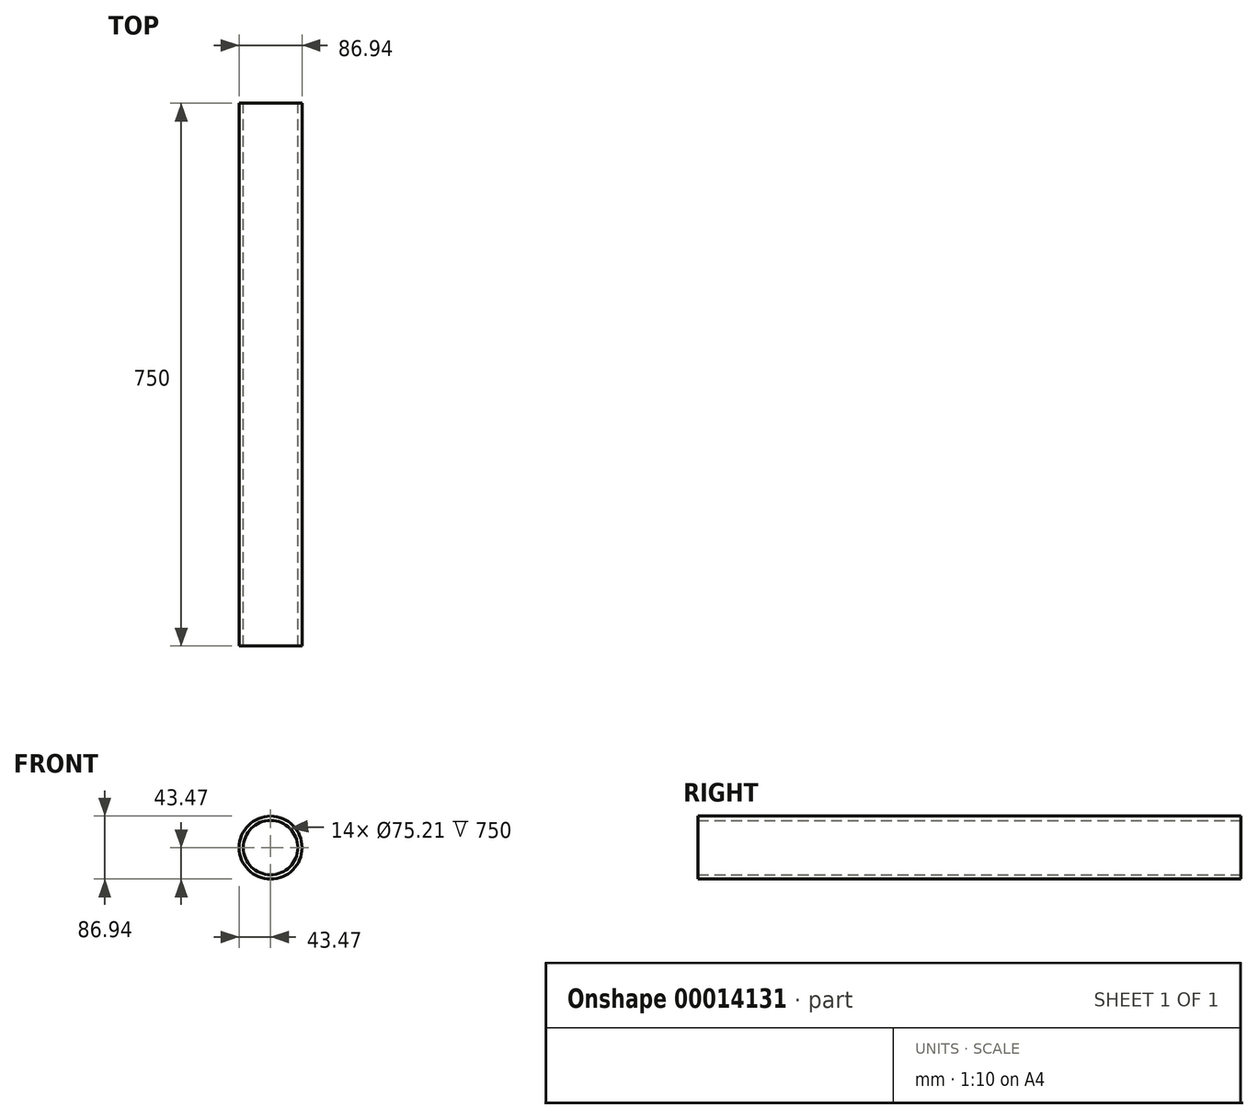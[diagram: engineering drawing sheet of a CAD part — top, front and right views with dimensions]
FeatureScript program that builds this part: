
annotation { "Feature Type Name" : "Feature", "Feature Type Description" : "" }
export const myFeature = defineFeature(function(context is Context, id is Id, definition is map)
    precondition{}
    {
        {
            var Q0;
            Q0=qCreatedBy(makeId("Front.planeOp"),FACE);
            var sketch = newSketch(context, id + "F0", { "sketchPlane" : qUnion([Q0])});
            skCircle(sketch, "E0", {"center": v(0, 0) * mm, "radius": 43.47 * mm});
            skLineSegment(sketch, "E1", {"start": v(0, 0) * mm, "end": v(0, 43.47) * mm, "construction": true});
            skCircle(sketch, "E2", {"center": v(0, 0) * mm, "radius": 37.6 * mm});
            skSolve(sketch);
        }
        {
            var Q0;
            Q0=makeQuery(id+"F0.imprint","IMPRINT",FACE,{"disambiguationData":[TD([[makeQuery(id+"F0.imprint","IMPRINT",EDGE,{"derivedFrom":sQuery(id+"F0.wireOp",EDGE,"E0")}),1.0]])]});
            var Q1;
            Q1=sQuery(id+"F0.wireOp",EDGE,"E0");
            var Q2;
            Q2=sQuery(id+"F0.wireOp",EDGE,"E2");
            extrude(context, id + "F1", {"entities" : qUnion([Q0]), "surfaceEntities" : qUnion([Q1, Q2]), "endBound" : BoundingType.SYMMETRIC, "depth" : 750 * mm});
        }
    });
